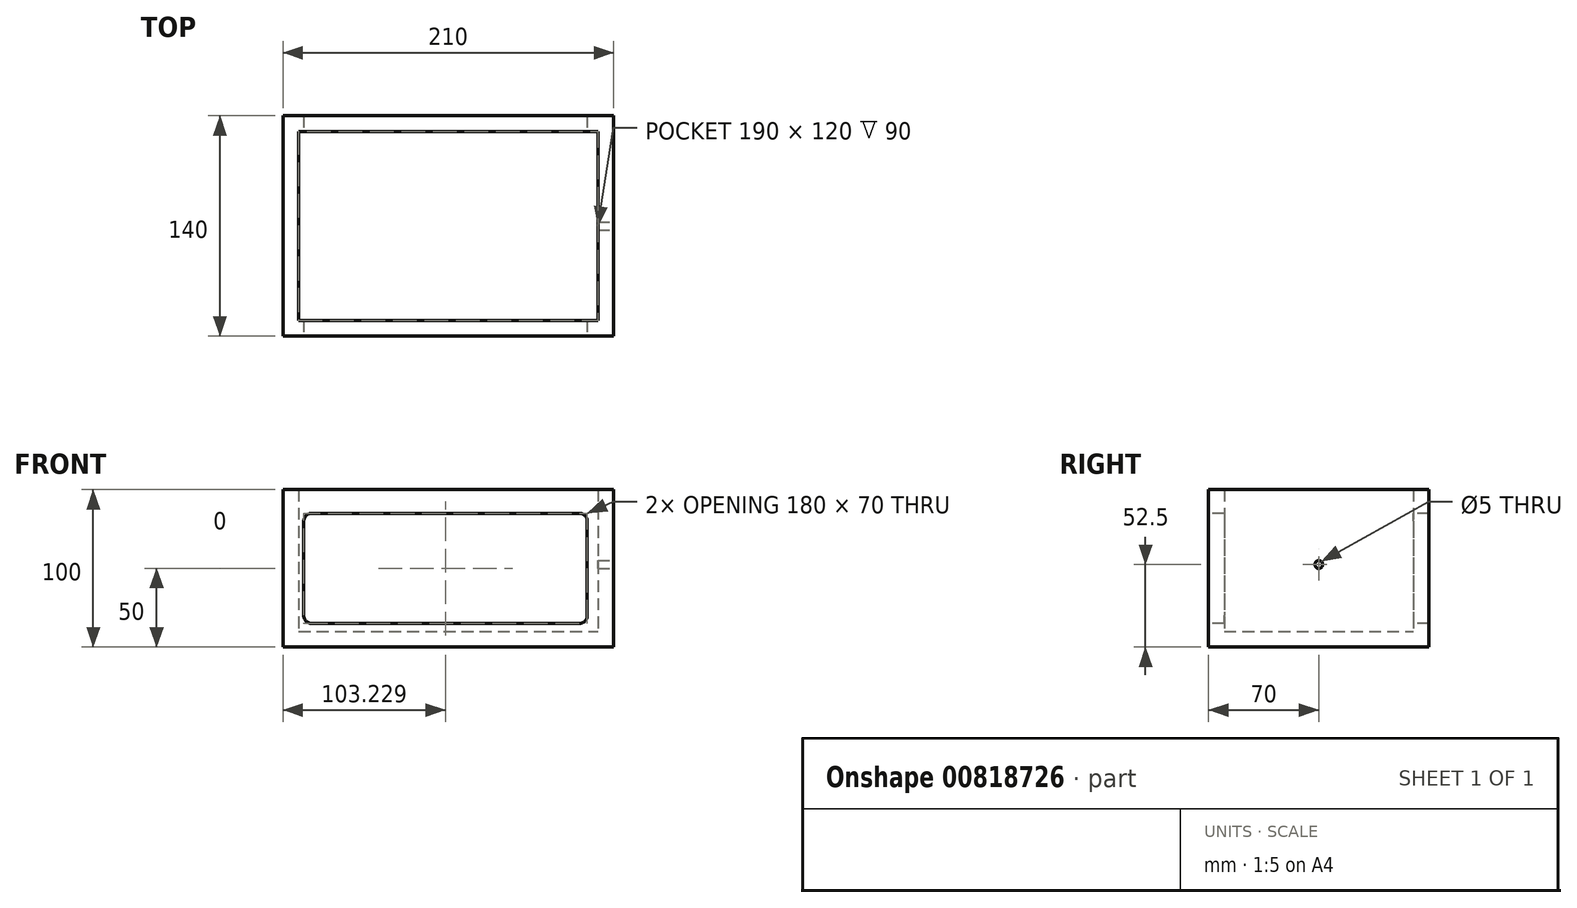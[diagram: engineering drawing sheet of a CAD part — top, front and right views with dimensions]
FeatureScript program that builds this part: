
annotation { "Feature Type Name" : "Feature", "Feature Type Description" : "" }
export const myFeature = defineFeature(function(context is Context, id is Id, definition is map)
    precondition{}
    {
        {
            var Q0;
            Q0=qCreatedBy(makeId("Top.planeOp"),FACE);
            var sketch = newSketch(context, id + "F0", { "sketchPlane" : qUnion([Q0])});
            skLineSegment(sketch, "E0.bottom", {"start": v(-105, -70) * mm, "end": v(105, -70) * mm});
            skLineSegment(sketch, "E0.top", {"start": v(-105, 70) * mm, "end": v(105, 70) * mm});
            skLineSegment(sketch, "E0.left", {"start": v(-105, -70) * mm, "end": v(-105, 70) * mm});
            skLineSegment(sketch, "E0.right", {"start": v(105, -70) * mm, "end": v(105, 70) * mm});
            skPoint(sketch, "E0.middle", {"position": v(0, 0) * mm});
            skLineSegment(sketch, "E1.0", {"start": v(95, -60) * mm, "end": v(95, 60) * mm});
            skLineSegment(sketch, "E1.1", {"start": v(-95, -60) * mm, "end": v(95, -60) * mm});
            skLineSegment(sketch, "E1.2", {"start": v(-95, -60) * mm, "end": v(-95, 60) * mm});
            skLineSegment(sketch, "E1.3", {"start": v(-95, 60) * mm, "end": v(95, 60) * mm});
            skLineSegment(sketch, "E2.bottom", {"start": v(72.66, -60) * mm, "end": v(82.66, -60) * mm});
            skLineSegment(sketch, "E2.top", {"start": v(72.66, 60) * mm, "end": v(82.66, 60) * mm});
            skSolve(sketch);
        }
        {
            var Q0;
            Q0=makeQuery(id+"F0.imprint","IMPRINT",FACE,{"disambiguationData":[TD([[makeQuery(id+"F0.imprint","IMPRINT",EDGE,{"derivedFrom":sQuery(id+"F0.wireOp",EDGE,"E1.0")}),1.0]])]});
            var Q1;
            {var subQ0=sQuery(id+"F0.wireOp",EDGE,"E1.2");Q1=makeQuery(id+"F0.imprint","IMPRINT",FACE,{"disambiguationData":[TD([[makeQuery(id+"F0.imprint","IMPRINT",EDGE,{"derivedFrom":subQ0}),-1.0]])]});}
            var Q2;
            Q2=makeQuery(id+"F0.imprint","IMPRINT",FACE,{"disambiguationData":[TD([[makeQuery(id+"F0.imprint","IMPRINT",EDGE,{"derivedFrom":sQuery(id+"F0.wireOp",EDGE,"E2.bottom")}),1.0]])]});
            extrude(context, id + "F1", {"entities" : qUnion([Q0, Q1, Q2]), "depth" : 10 * mm, "offsetDistance" : 25 * mm});
        }
        {
            var Q0;
            Q0=makeQuery(id+"F0.imprint","IMPRINT",FACE,{"disambiguationData":[TD([[makeQuery(id+"F0.imprint","IMPRINT",EDGE,{"derivedFrom":sQuery(id+"F0.wireOp",EDGE,"E0.bottom")}),1.0]])]});
            extrude(context, id + "F2", {"entities" : qUnion([Q0]), "operationType" : NewBodyOperationType.ADD, "depth" : 100 * mm, "offsetDistance" : 25 * mm});
        }
        {
            var Q0;
            Q0=makeQuery(id+"F2.opExtrude","SWEPT_FACE",FACE,{"disambiguationData":[OSD([sQuery(id+"F0.wireOp",EDGE,"E0.bottom")])]});
            var sketch = newSketch(context, id + "F3", { "sketchPlane" : qUnion([Q0])});
            skLineSegment(sketch, "E3", {"start": v(-105, 0) * mm, "end": v(-91.77, 15) * mm, "construction": true});
            skLineSegment(sketch, "E4", {"start": v(-105, 100) * mm, "end": v(-91.77, 85) * mm, "construction": true});
            skPoint(sketch, "E5.visualSharp", {"position": v(-91.77, 85) * mm});
            skPoint(sketch, "E6.visualSharp", {"position": v(-91.77, 15) * mm});
            skLineSegment(sketch, "E7.bottom", {"start": v(-91.77, 15) * mm, "end": v(88.23, 15) * mm});
            skLineSegment(sketch, "E7.top", {"start": v(-91.77, 85) * mm, "end": v(88.23, 85) * mm});
            skLineSegment(sketch, "E7.left", {"start": v(-91.77, 15) * mm, "end": v(-91.77, 85) * mm});
            skLineSegment(sketch, "E7.right", {"start": v(88.23, 15) * mm, "end": v(88.23, 85) * mm});
            skSolve(sketch);
        }
        {
            var Q0;
            Q0 = qSketchRegion(id + "F3", true);
            extrude(context, id + "F4", {"entities" : qUnion([Q0]), "operationType" : NewBodyOperationType.REMOVE, "oppositeDirection" : true, "depth" : 202.55 * mm, "offsetDistance" : 25 * mm});
        }
        {
            var Q0;
            Q0=makeQuery(id+"F2.opExtrude","SWEPT_FACE",FACE,{"disambiguationData":[OSD([sQuery(id+"F0.wireOp",EDGE,"E0.right")])]});
            var sketch = newSketch(context, id + "F5", { "sketchPlane" : qUnion([Q0])});
            skLineSegment(sketch, "E8.0", {"start": v(-70, 95) * mm, "end": v(70, 95) * mm, "construction": true});
            skLineSegment(sketch, "E9.0", {"start": v(60, 100) * mm, "end": v(60, 0) * mm, "construction": true});
            skLineSegment(sketch, "E10.0", {"start": v(-60, 100) * mm, "end": v(-60, 0) * mm, "construction": true});
            skLineSegment(sketch, "E11.0", {"start": v(-70, 10) * mm, "end": v(70, 10) * mm, "construction": true});
            skLineSegment(sketch, "E12", {"start": v(-60, 95) * mm, "end": v(60, 10) * mm, "construction": true});
            skLineSegment(sketch, "E13", {"start": v(-60, 10) * mm, "end": v(60, 95) * mm, "construction": true});
            skCircle(sketch, "E14", {"center": v(0, 52.5) * mm, "radius": 2.5 * mm});
            skSolve(sketch);
        }
        {
            var Q0;
            Q0=makeQuery(id+"F5.imprint","IMPRINT",FACE,{"disambiguationData":[TD([[makeQuery(id+"F5.imprint","IMPRINT",EDGE,{"derivedFrom":sQuery(id+"F5.wireOp",EDGE,"E14")}),1.0]])]});
            extrude(context, id + "F6", {"entities" : qUnion([Q0]), "operationType" : NewBodyOperationType.REMOVE, "oppositeDirection" : true, "depth" : 10 * mm, "offsetDistance" : 25 * mm});
        }
        {
            var Q0;
            {var subQ0=sQuery(id+"F3.wireOp",EDGE,"E7.bottom");var subQ1=sQuery(id+"F3.wireOp",EDGE,"E7.left");Q0=makeQuery(id+"F4.boolean.opBoolean","COPY",EDGE,{"disambiguationData":[TD([makeQuery(id+"F2.opExtrude","SWEPT_FACE",FACE,{"disambiguationData":[OSD([sQuery(id+"F0.wireOp",EDGE,"E0.bottom")])]})])],"derivedFrom":makeQuery(id+"F4.opExtrude","SWEPT_EDGE",EDGE,{"disambiguationData":[OSD([subQ0,subQ1])]})});}
            var Q1;
            {var subQ0=sQuery(id+"F3.wireOp",EDGE,"E7.top");var subQ1=sQuery(id+"F3.wireOp",EDGE,"E7.left");Q1=makeQuery(id+"F4.boolean.opBoolean","COPY",EDGE,{"disambiguationData":[TD([makeQuery(id+"F2.opExtrude","SWEPT_FACE",FACE,{"disambiguationData":[OSD([sQuery(id+"F0.wireOp",EDGE,"E0.bottom")])]})])],"derivedFrom":makeQuery(id+"F4.opExtrude","SWEPT_EDGE",EDGE,{"disambiguationData":[OSD([subQ0,subQ1])]})});}
            var Q2;
            {var subQ0=sQuery(id+"F3.wireOp",EDGE,"E7.bottom");var subQ1=sQuery(id+"F3.wireOp",EDGE,"E7.right");Q2=makeQuery(id+"F4.boolean.opBoolean","COPY",EDGE,{"disambiguationData":[TD([makeQuery(id+"F2.opExtrude","SWEPT_FACE",FACE,{"disambiguationData":[OSD([sQuery(id+"F0.wireOp",EDGE,"E0.bottom")])]})])],"derivedFrom":makeQuery(id+"F4.opExtrude","SWEPT_EDGE",EDGE,{"disambiguationData":[OSD([subQ0,subQ1])]})});}
            var Q3;
            {var subQ0=sQuery(id+"F3.wireOp",EDGE,"E7.top");var subQ1=sQuery(id+"F3.wireOp",EDGE,"E7.right");Q3=makeQuery(id+"F4.boolean.opBoolean","COPY",EDGE,{"disambiguationData":[TD([makeQuery(id+"F2.opExtrude","SWEPT_FACE",FACE,{"disambiguationData":[OSD([sQuery(id+"F0.wireOp",EDGE,"E0.bottom")])]})])],"derivedFrom":makeQuery(id+"F4.opExtrude","SWEPT_EDGE",EDGE,{"disambiguationData":[OSD([subQ0,subQ1])]})});}
            var Q4;
            {var subQ0=sQuery(id+"F3.wireOp",EDGE,"E7.left");var subQ1=sQuery(id+"F3.wireOp",EDGE,"E7.top");Q4=makeQuery(id+"F4.boolean.opBoolean","COPY",EDGE,{"disambiguationData":[TD([makeQuery(id+"F2.opExtrude","SWEPT_FACE",FACE,{"disambiguationData":[OSD([sQuery(id+"F0.wireOp",EDGE,"E0.top")])]})])],"derivedFrom":makeQuery(id+"F4.opExtrude","SWEPT_EDGE",EDGE,{"disambiguationData":[OSD([subQ1,subQ0])]})});}
            var Q5;
            {var subQ0=sQuery(id+"F3.wireOp",EDGE,"E7.left");var subQ1=sQuery(id+"F3.wireOp",EDGE,"E7.bottom");Q5=makeQuery(id+"F4.boolean.opBoolean","COPY",EDGE,{"disambiguationData":[TD([makeQuery(id+"F2.opExtrude","SWEPT_FACE",FACE,{"disambiguationData":[OSD([sQuery(id+"F0.wireOp",EDGE,"E0.top")])]})])],"derivedFrom":makeQuery(id+"F4.opExtrude","SWEPT_EDGE",EDGE,{"disambiguationData":[OSD([subQ1,subQ0])]})});}
            var Q6;
            {var subQ0=sQuery(id+"F3.wireOp",EDGE,"E7.bottom");var subQ1=sQuery(id+"F3.wireOp",EDGE,"E7.right");Q6=makeQuery(id+"F4.boolean.opBoolean","COPY",EDGE,{"disambiguationData":[TD([makeQuery(id+"F2.opExtrude","SWEPT_FACE",FACE,{"disambiguationData":[OSD([sQuery(id+"F0.wireOp",EDGE,"E0.top")])]})])],"derivedFrom":makeQuery(id+"F4.opExtrude","SWEPT_EDGE",EDGE,{"disambiguationData":[OSD([subQ0,subQ1])]})});}
            var Q7;
            {var subQ0=sQuery(id+"F3.wireOp",EDGE,"E7.right");var subQ1=sQuery(id+"F3.wireOp",EDGE,"E7.top");Q7=makeQuery(id+"F4.boolean.opBoolean","COPY",EDGE,{"disambiguationData":[TD([makeQuery(id+"F2.opExtrude","SWEPT_FACE",FACE,{"disambiguationData":[OSD([sQuery(id+"F0.wireOp",EDGE,"E0.top")])]})])],"derivedFrom":makeQuery(id+"F4.opExtrude","SWEPT_EDGE",EDGE,{"disambiguationData":[OSD([subQ1,subQ0])]})});}
            fillet(context, id + "F7", {"entities" : qUnion([Q0, Q1, Q2, Q3, Q4, Q5, Q6, Q7]), "radius" : 5 * mm, "tangentPropagation" : true, "allowEdgeOverflow" : false});
        }
    });
